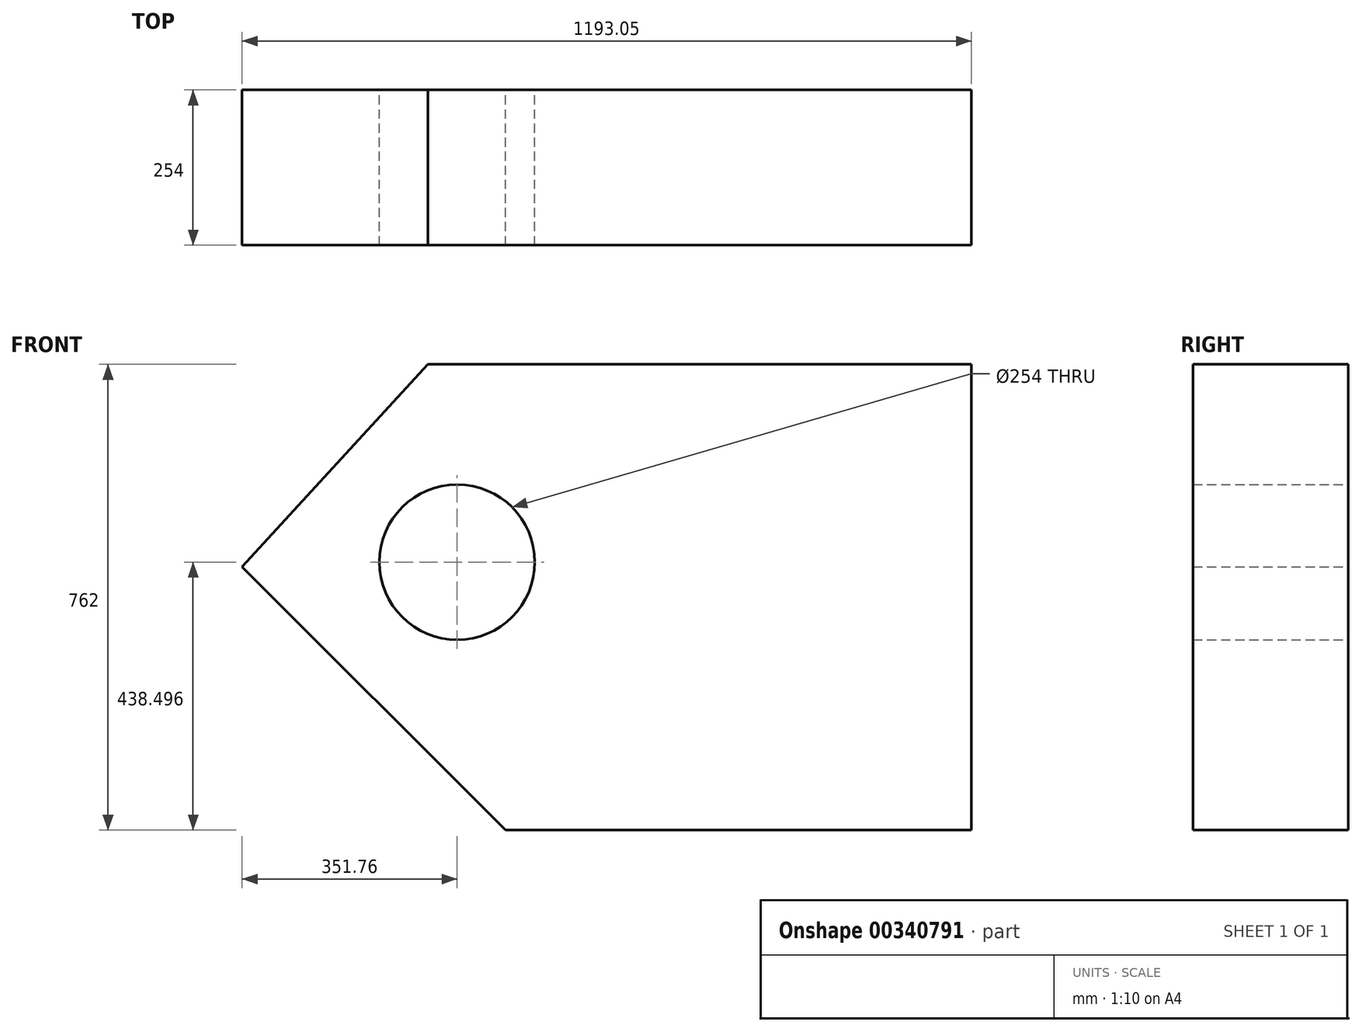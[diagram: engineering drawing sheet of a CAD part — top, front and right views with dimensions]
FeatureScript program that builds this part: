
annotation { "Feature Type Name" : "Feature", "Feature Type Description" : "" }
export const myFeature = defineFeature(function(context is Context, id is Id, definition is map)
    precondition{}
    {
        {
            var Q0;
            Q0=qCreatedBy(makeId("Front.planeOp"),FACE);
            var sketch = newSketch(context, id + "F0", { "sketchPlane" : qUnion([Q0])});
            skLineSegment(sketch, "E0", {"start": v(-47.71, -58.6) * mm, "end": v(841.29, -58.6) * mm});
            skLineSegment(sketch, "E1", {"start": v(841.29, -58.6) * mm, "end": v(841.29, -820.6) * mm});
            skLineSegment(sketch, "E2", {"start": v(841.29, -820.6) * mm, "end": v(79.29, -820.6) * mm});
            skLineSegment(sketch, "E3", {"start": v(79.29, -820.6) * mm, "end": v(-351.76, -389.54) * mm});
            skLineSegment(sketch, "E4", {"start": v(-351.76, -389.54) * mm, "end": v(-47.71, -58.6) * mm});
            skCircle(sketch, "E5", {"center": v(0, -382.1) * mm, "radius": 127 * mm});
            skSolve(sketch);
        }
        {
            var Q0;
            Q0=makeQuery(id+"F0.imprint","IMPRINT",FACE,{"disambiguationData":[TD([[makeQuery(id+"F0.imprint","IMPRINT",EDGE,{"derivedFrom":sQuery(id+"F0.wireOp",EDGE,"E0")}),-1.0]])]});
            extrude(context, id + "F1", {"entities" : qUnion([Q0]), "depth" : 254 * mm});
        }
    });
